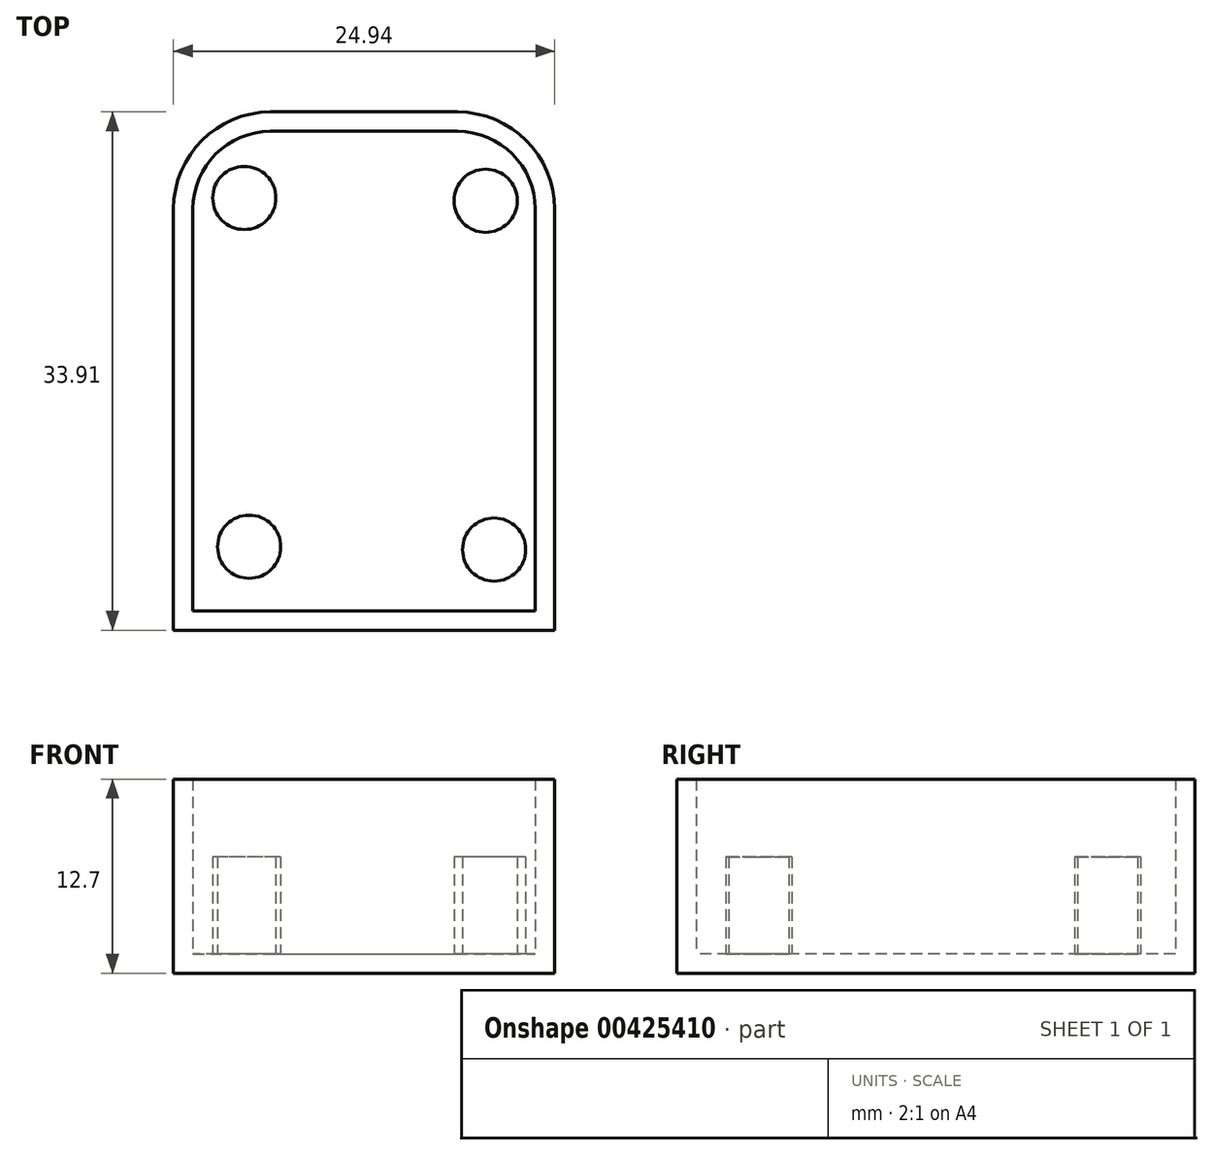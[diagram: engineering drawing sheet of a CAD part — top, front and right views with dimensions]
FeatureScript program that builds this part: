
annotation { "Feature Type Name" : "Feature", "Feature Type Description" : "" }
export const myFeature = defineFeature(function(context is Context, id is Id, definition is map)
    precondition{}
    {
        {
            var Q0;
            Q0=qCreatedBy(makeId("Top.planeOp"),FACE);
            var sketch = newSketch(context, id + "F0", { "sketchPlane" : qUnion([Q0])});
            skLineSegment(sketch, "E0.bottom", {"start": v(6.35, 0) * mm, "end": v(18.6, 0) * mm});
            skLineSegment(sketch, "E0.top", {"start": v(0, -33.91) * mm, "end": v(24.94, -33.91) * mm});
            skLineSegment(sketch, "E0.left", {"start": v(0, -6.35) * mm, "end": v(0, -33.91) * mm});
            skLineSegment(sketch, "E0.right", {"start": v(24.94, -6.35) * mm, "end": v(24.94, -33.91) * mm});
            skPoint(sketch, "E1.visualSharp", {"position": v(0, 0) * mm});
            skArc(sketch, "E1.filletArc", {"start": v(6.35, 0) * mm, "mid": v(1.86, -1.86) * mm, "end": v(0, -6.35) * mm});
            skPoint(sketch, "E2.visualSharp", {"position": v(24.94, 0) * mm});
            skArc(sketch, "E2.filletArc", {"start": v(24.94, -6.35) * mm, "mid": v(23.08, -1.86) * mm, "end": v(18.6, 0) * mm});
            skSolve(sketch);
        }
        {
            var Q0;
            Q0 = qSketchRegion(id + "F0", true);
            extrude(context, id + "F1", {"entities" : qUnion([Q0]), "depth" : 12.7 * mm});
        }
        {
            var Q0;
            Q0=makeQuery(id+"F1.opExtrude","CAP_FACE",FACE,{"disambiguationData":[OSD([sQuery(id+"F0.wireOp",EDGE,"E0.bottom"),sQuery(id+"F0.wireOp",EDGE,"E0.top"),sQuery(id+"F0.wireOp",EDGE,"E0.left"),sQuery(id+"F0.wireOp",EDGE,"E0.right"),sQuery(id+"F0.wireOp",EDGE,"E1.filletArc"),sQuery(id+"F0.wireOp",EDGE,"E2.filletArc")])],"isStart":false});
            shell(context, id + "F2", {"entities" : qUnion([Q0]), "thickness" : 1.27 * mm});
        }
        {
            var Q0;
            Q0=makeQuery(id+"F2.opShell","OFFSET_FACE",FACE,{"disambiguationData":[OSD([sQuery(id+"F0.wireOp",EDGE,"E0.bottom"),sQuery(id+"F0.wireOp",EDGE,"E0.top"),sQuery(id+"F0.wireOp",EDGE,"E0.left"),sQuery(id+"F0.wireOp",EDGE,"E0.right"),sQuery(id+"F0.wireOp",EDGE,"E1.filletArc"),sQuery(id+"F0.wireOp",EDGE,"E2.filletArc")])]});
            var sketch = newSketch(context, id + "F3", { "sketchPlane" : qUnion([Q0])});
            skCircle(sketch, "E3", {"center": v(4.63, -5.63) * mm, "radius": 2.07 * mm});
            skSolve(sketch);
        }
        {
            var Q0;
            Q0 = qSketchRegion(id + "F3", true);
            extrude(context, id + "F4", {"entities" : qUnion([Q0]), "operationType" : NewBodyOperationType.ADD, "depth" : 6.35 * mm});
        }
        {
            var Q0;
            Q0=makeQuery(id+"F2.opShell","OFFSET_FACE",FACE,{"disambiguationData":[OSD([sQuery(id+"F0.wireOp",EDGE,"E0.bottom"),sQuery(id+"F0.wireOp",EDGE,"E0.top"),sQuery(id+"F0.wireOp",EDGE,"E0.left"),sQuery(id+"F0.wireOp",EDGE,"E0.right"),sQuery(id+"F0.wireOp",EDGE,"E1.filletArc"),sQuery(id+"F0.wireOp",EDGE,"E2.filletArc")])]});
            var sketch = newSketch(context, id + "F5", { "sketchPlane" : qUnion([Q0])});
            skCircle(sketch, "E4", {"center": v(4.95, -28.45) * mm, "radius": 2.07 * mm});
            skCircle(sketch, "E5", {"center": v(20.43, -5.81) * mm, "radius": 2.07 * mm});
            skCircle(sketch, "E6", {"center": v(20.98, -28.64) * mm, "radius": 2.07 * mm});
            skSolve(sketch);
        }
        {
            var Q0;
            Q0 = qSketchRegion(id + "F5", true);
            extrude(context, id + "F6", {"entities" : qUnion([Q0]), "operationType" : NewBodyOperationType.ADD, "depth" : 6.35 * mm});
        }
    });
